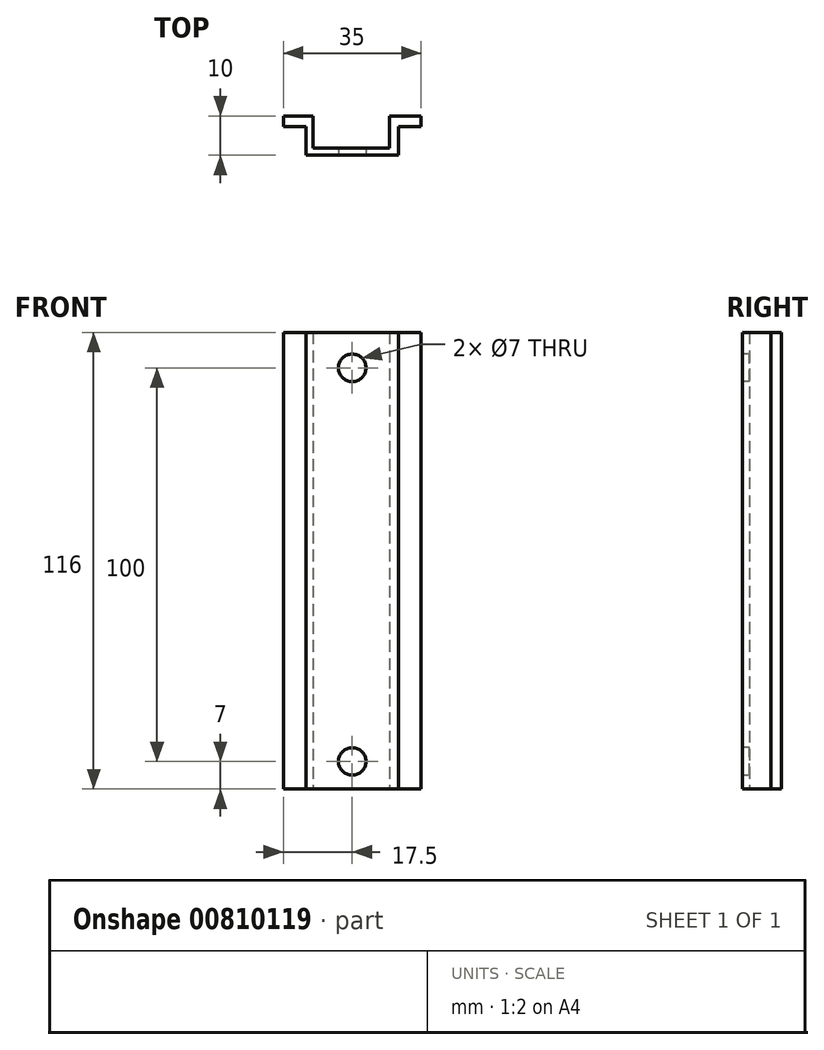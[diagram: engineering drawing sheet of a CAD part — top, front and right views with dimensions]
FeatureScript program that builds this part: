
annotation { "Feature Type Name" : "Feature", "Feature Type Description" : "" }
export const myFeature = defineFeature(function(context is Context, id is Id, definition is map)
    precondition{}
    {
        {
            var Q0;
            Q0=qCreatedBy(makeId("Top.planeOp"),FACE);
            var sketch = newSketch(context, id + "F0", { "sketchPlane" : qUnion([Q0])});
            skLineSegment(sketch, "E0.bottom", {"start": v(-17.5, 5) * mm, "end": v(17.5, 5) * mm});
            skLineSegment(sketch, "E0.top", {"start": v(-17.5, -5) * mm, "end": v(17.5, -5) * mm});
            skLineSegment(sketch, "E0.left", {"start": v(-17.5, 5) * mm, "end": v(-17.5, -5) * mm});
            skLineSegment(sketch, "E0.right", {"start": v(17.5, 5) * mm, "end": v(17.5, -5) * mm});
            skPoint(sketch, "E0.middle", {"position": v(0, 0) * mm});
            skLineSegment(sketch, "E1.bottom", {"start": v(-17.5, 2.3) * mm, "end": v(-11.73, 2.3) * mm});
            skLineSegment(sketch, "E1.top", {"start": v(-17.5, -5) * mm, "end": v(-11.73, -5) * mm});
            skLineSegment(sketch, "E1.left", {"start": v(-17.5, 2.3) * mm, "end": v(-17.5, -5) * mm});
            skLineSegment(sketch, "E1.right", {"start": v(-11.73, 2.3) * mm, "end": v(-11.73, -5) * mm});
            skLineSegment(sketch, "E2.MirrorCS", {"start": v(17.5, 2.3) * mm, "end": v(11.73, 2.3) * mm});
            skLineSegment(sketch, "E3.MirrorCS", {"start": v(11.73, 2.3) * mm, "end": v(11.73, -5) * mm});
            skLineSegment(sketch, "E4.bottom", {"start": v(-9.92, 5) * mm, "end": v(9.42, 5) * mm});
            skLineSegment(sketch, "E4.top", {"start": v(-9.92, -3.22) * mm, "end": v(9.42, -3.22) * mm});
            skLineSegment(sketch, "E4.left", {"start": v(-9.92, 5) * mm, "end": v(-9.92, -3.22) * mm});
            skLineSegment(sketch, "E4.right", {"start": v(9.42, 5) * mm, "end": v(9.42, -3.22) * mm});
            skSolve(sketch);
        }
        {
            var Q0;
            {var subQ1=sQuery(id+"F0.wireOp",EDGE,"E1.bottom");Q0=makeQuery(id+"F0.imprint","IMPRINT",FACE,{"disambiguationData":[TD([[makeQuery(id+"F0.imprint","IMPRINT",EDGE,{"derivedFrom":subQ1}),1.0]])]});}
            extrude(context, id + "F1", {"entities" : qUnion([Q0]), "depth" : 116 * mm, "offsetDistance" : 25 * mm});
        }
        {
            var Q0;
            Q0=makeQuery(id+"F1.opExtrude","SWEPT_FACE",FACE,{"disambiguationData":[OSD([sQuery(id+"F0.wireOp",EDGE,"E4.top")])]});
            var sketch = newSketch(context, id + "F2", { "sketchPlane" : qUnion([Q0])});
            skPoint(sketch, "E5", {"position": v(0, 107) * mm});
            skPoint(sketch, "E6", {"position": v(0, 7) * mm});
            skSolve(sketch);
        }
        {
            var Q0;
            Q0=sQuery(id+"F2.wireOp",VERTEX,"E5");
            var Q1;
            Q1=sQuery(id+"F2.wireOp",VERTEX,"E6");
            var Q2;
            Q2=makeQuery(id+"F1.opExtrude","SWEPT_BODY",BODY,{"disambiguationData":[OSD([sQuery(id+"F0.wireOp",EDGE,"E0.bottom"),sQuery(id+"F0.wireOp",EDGE,"E0.top"),sQuery(id+"F0.wireOp",EDGE,"E0.left"),sQuery(id+"F0.wireOp",EDGE,"E0.right"),sQuery(id+"F0.wireOp",EDGE,"E1.bottom"),sQuery(id+"F0.wireOp",EDGE,"E1.right"),sQuery(id+"F0.wireOp",EDGE,"E2.MirrorCS"),sQuery(id+"F0.wireOp",EDGE,"E3.MirrorCS"),sQuery(id+"F0.wireOp",EDGE,"E4.top"),sQuery(id+"F0.wireOp",EDGE,"E4.left"),sQuery(id+"F0.wireOp",EDGE,"E4.right")])]});
            hole(context, id + "F3", {"style" : HoleStyle.SIMPLE, "endStyle" : HoleEndStyle.BLIND, "holeDiameter" : 7 * mm, "majorDiameter" : 5 * mm, "holeDepth" : 14.4 * mm, "isTappedThrough" : true, "tappedDepth" : 12 * mm, "tapClearance" : 3, "locations" : qUnion([Q0, Q1]), "scope" : qUnion([Q2])});
        }
    });
